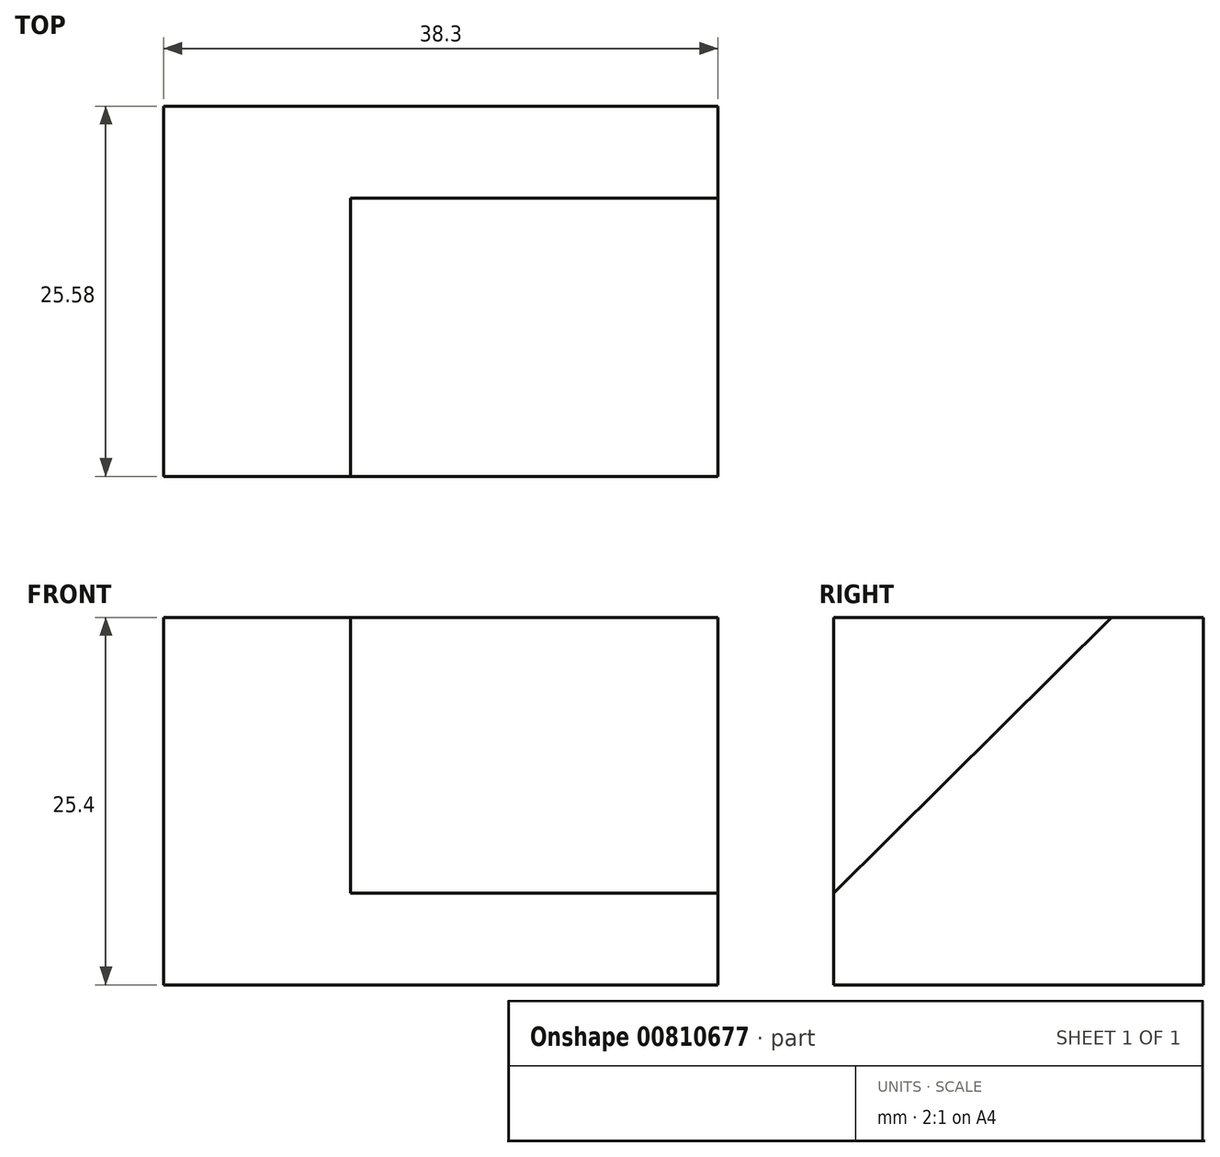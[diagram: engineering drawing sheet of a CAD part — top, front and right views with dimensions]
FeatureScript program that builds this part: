
annotation { "Feature Type Name" : "Feature", "Feature Type Description" : "" }
export const myFeature = defineFeature(function(context is Context, id is Id, definition is map)
    precondition{}
    {
        {
            var Q0;
            Q0=qCreatedBy(makeId("Top.planeOp"),FACE);
            var sketch = newSketch(context, id + "F0", { "sketchPlane" : qUnion([Q0])});
            skLineSegment(sketch, "E0.bottom", {"start": v(0, 0) * mm, "end": v(38.3, 0) * mm});
            skLineSegment(sketch, "E0.top", {"start": v(0, 25.58) * mm, "end": v(38.3, 25.58) * mm});
            skLineSegment(sketch, "E0.left", {"start": v(0, 0) * mm, "end": v(0, 25.58) * mm});
            skLineSegment(sketch, "E0.right", {"start": v(38.3, 0) * mm, "end": v(38.3, 25.58) * mm});
            skSolve(sketch);
        }
        {
            var Q0;
            Q0 = qSketchRegion(id + "F0", true);
            extrude(context, id + "F1", {"entities" : qUnion([Q0]), "depth" : 25.4 * mm, "offsetDistance" : 25.4 * mm});
        }
        {
            var Q0;
            Q0=makeQuery(id+"F1.opExtrude","SWEPT_FACE",FACE,{"disambiguationData":[OSD([sQuery(id+"F0.wireOp",EDGE,"E0.right")])]});
            var sketch = newSketch(context, id + "F2", { "sketchPlane" : qUnion([Q0])});
            skLineSegment(sketch, "E1", {"start": v(25.58, 25.4) * mm, "end": v(19.23, 25.4) * mm});
            skLineSegment(sketch, "E2", {"start": v(0, 0) * mm, "end": v(0, 6.35) * mm});
            skLineSegment(sketch, "E3", {"start": v(0, 6.35) * mm, "end": v(19.23, 25.4) * mm});
            skSolve(sketch);
        }
        {
            var Q0;
            {var subQ0=sQuery(id+"F2.wireOp",EDGE,"E3");Q0=makeQuery(id+"F2.imprint","IMPRINT",FACE,{"disambiguationData":[TD([[makeQuery(id+"F2.imprint","IMPRINT",EDGE,{"derivedFrom":subQ0}),1.0]])]});}
            extrude(context, id + "F3", {"entities" : qUnion([Q0]), "operationType" : NewBodyOperationType.REMOVE, "oppositeDirection" : true, "depth" : 25.4 * mm, "offsetDistance" : 25.4 * mm});
        }
    });
